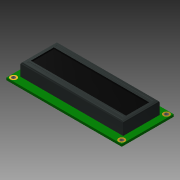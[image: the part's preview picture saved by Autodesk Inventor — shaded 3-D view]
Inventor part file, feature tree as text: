
AUTODESK INVENTOR PART (.ipt)
format: ipt  version: 2013 (Build 170138000, 138)  size: 270,336 bytes
history: native  units: mm
features: sketch x8, extrude x6, pattern_linear x3, hole x2, fillet x2
ambient origin geometry x8: Origin, YZ Plane, XZ Plane, XY Plane, X Axis, Y Axis, Z Axis, Center Point
bodies: Solid1 (feature_tree)
feature tree (21):
  extrude  "Extrusion1"  Depth=36.0mm
  hole  "Hole1"  [1 undecoded]
  extrude  "Extrusion2"  Depth=2.5mm
  extrude  "Extrusion3"  Depth=75.0mm
  fillet  "Fillet1"  Radius=25.2mm
  extrude  "Extrusion4"  Depth=8.6mm TaperAngle=0.0deg
  fillet  "Fillet2"  Radius=66.0mm
  extrude  "Extrusion5"  Depth=1.0mm TaperAngle=0.0deg
  pattern_linear  "Rectangular Pattern1"  Spacing1=0.6mm  [1 undecoded]
  hole  "Hole4"  [1 undecoded]
  pattern_linear  "Rectangular Pattern2"  Spacing1=1.6mm  [1 undecoded]
  extrude  "Extrusion6"  Depth=1.6mm
  pattern_linear  "Rectangular Pattern3"  Spacing1=1.5mm  [1 undecoded]
  sketch  "Sketch1"  dims[d0=80.0mm d2=36.0mm]
  sketch  "Sketch2"  dims[d3=1.6mm d4=0.0mm d5=2.5mm]
  sketch  "Sketch3"  dims[d6=2.5mm d7=2.5mm]
  sketch  "Sketch4"  dims[d8=2.5mm d9=75.0mm]
  sketch  "Sketch5"  dims[d10=2.5mm d11=6.0mm d12=4.0mm d13=2.0mm d14=90.0deg d15=8.0mm d16=20.594885mm d17=25.2mm]
  sketch  "Sketch8"  dims[d19=71.2mm d20=8.6mm d21=0.0mm d22=66.0mm]
  sketch  "Sketch10"  dims[d24=16.0mm d25=1.0mm d26=0.0mm]
  sketch  "Sketch11"  dims[d27=1.0mm d28=0.6mm d30=1.5mm d31=1.6mm d32=1.6mm d33=1.5mm d34=0.6mm d35=0.1mm d36=0.0mm d37=1.0mm d56=1.8mm d58=2.5mm d59=8.0mm d60=0.01mm d61=0.0mm d62=160.0mm d64=2.54mm d74=1.0mm d76=1.0mm d77=6.0mm d78=4.0mm d79=2.0mm d80=90.0deg d81=8.0mm d82=20.594885mm d83=160.0mm d85=2.54mm d86=4.5mm d89=0.01mm d90=0.0mm d91=20.0mm d93=31.0mm d94=20.0mm d96=75.0mm]
note: 5 required parameter values undecoded (feature->parameter linkage not recoverable at this tier; creation-order binding heuristic only, values carry confidence <= 0.55)
